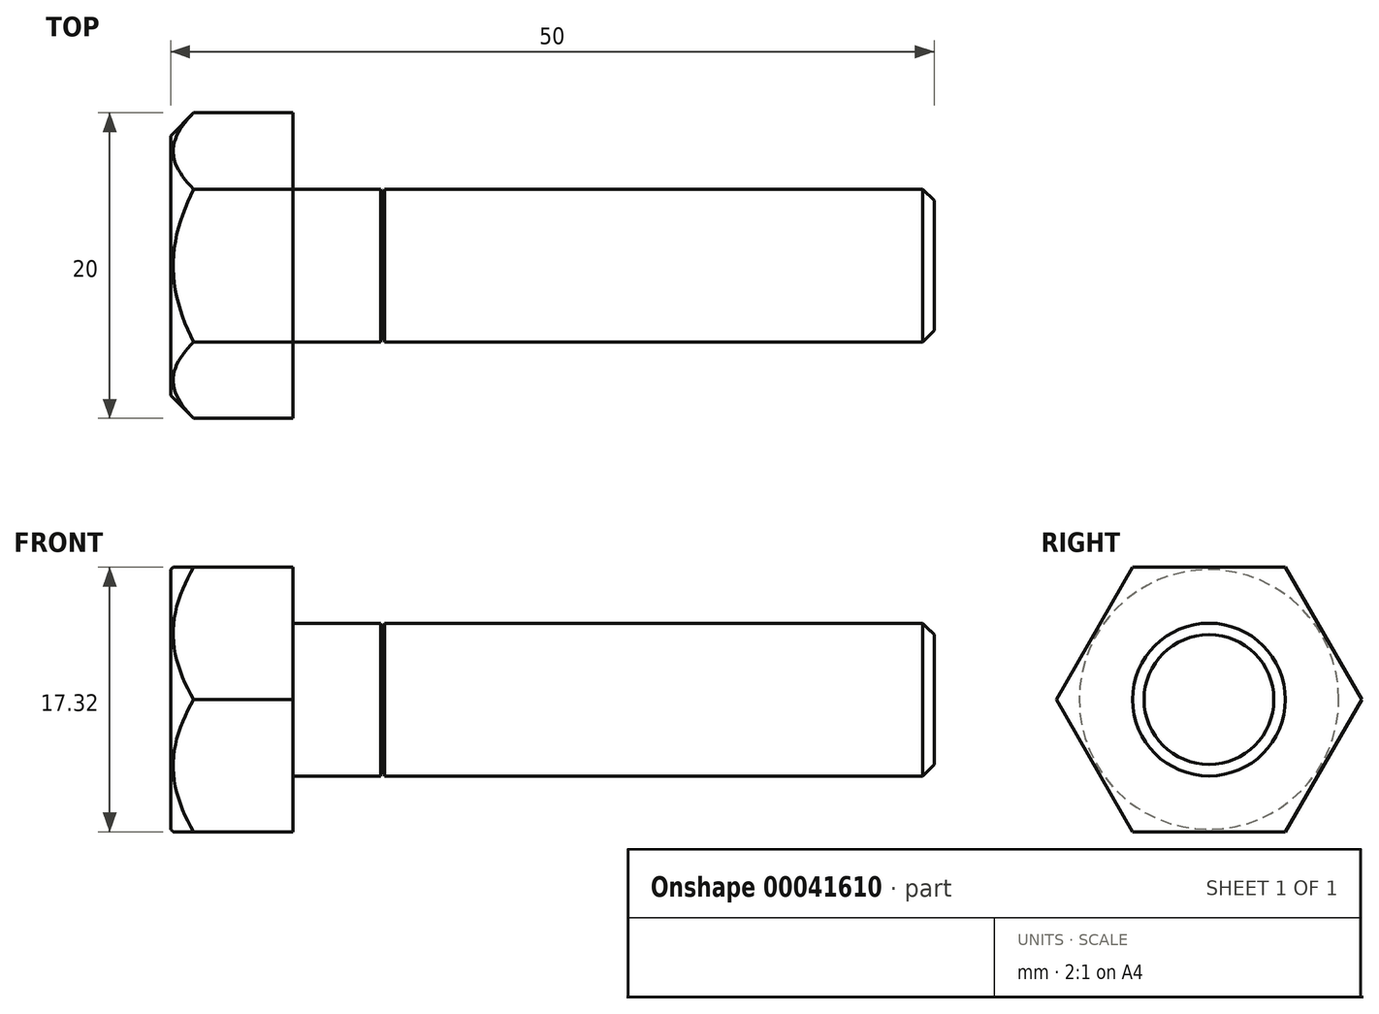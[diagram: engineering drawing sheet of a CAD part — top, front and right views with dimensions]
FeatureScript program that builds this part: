
annotation { "Feature Type Name" : "Feature", "Feature Type Description" : "" }
export const myFeature = defineFeature(function(context is Context, id is Id, definition is map)
    precondition{}
    {
        {
            var Q0;
            Q0=qCreatedBy(makeId("Front.planeOp"),FACE);
            var sketch = newSketch(context, id + "F0", { "sketchPlane" : qUnion([Q0])});
            skLineSegment(sketch, "E0.rect.bottom", {"start": v(8, 10) * mm, "end": v(0, 10) * mm});
            skLineSegment(sketch, "E0.rect.top", {"start": v(50, -10) * mm, "end": v(0, -10) * mm, "construction": true});
            skLineSegment(sketch, "E0.rect.left", {"start": v(50, 10) * mm, "end": v(50, -10) * mm, "construction": true});
            skLineSegment(sketch, "E0.rect.right", {"start": v(0, 10) * mm, "end": v(0, -10) * mm, "construction": true});
            skPoint(sketch, "E0.rect.middle", {"position": v(25, 0) * mm});
            skLineSegment(sketch, "E1", {"start": v(0, 0) * mm, "end": v(50, 0) * mm});
            skLineSegment(sketch, "E2", {"start": v(0, 10) * mm, "end": v(0, 0) * mm});
            skLineSegment(sketch, "E3", {"start": v(50, 4.25) * mm, "end": v(50, 0) * mm});
            skLineSegment(sketch, "E4", {"start": v(8, 10) * mm, "end": v(8, 5) * mm});
            skLineSegment(sketch, "E5", {"start": v(8, 5) * mm, "end": v(13.75, 5) * mm});
            skLineSegment(sketch, "E6", {"start": v(13.75, 5) * mm, "end": v(13.87, 4.25) * mm});
            skLineSegment(sketch, "E7", {"start": v(13.87, 4.25) * mm, "end": v(14, 5) * mm});
            skLineSegment(sketch, "E8", {"start": v(14, 5) * mm, "end": v(49.25, 5) * mm});
            skLineSegment(sketch, "E9", {"start": v(49.25, 5) * mm, "end": v(50, 4.25) * mm});
            skLineSegment(sketch, "E10", {"start": v(13.87, 4.25) * mm, "end": v(50, 4.25) * mm, "construction": true});
            skLineSegment(sketch, "E11", {"start": v(49.25, 5) * mm, "end": v(50, 5.75) * mm, "construction": true});
            skPoint(sketch, "E12", {"position": v(50, 4.25) * mm});
            skPoint(sketch, "E13", {"position": v(49.25, 5) * mm});
            skPoint(sketch, "E14", {"position": v(50, -4.25) * mm});
            skLineSegment(sketch, "E15", {"start": v(50, 0) * mm, "end": v(50, -4.25) * mm});
            skLineSegment(sketch, "E16", {"start": v(49.25, 5) * mm, "end": v(49.25, -5) * mm, "construction": true});
            skPoint(sketch, "E17", {"position": v(49.25, 0) * mm});
            skSolve(sketch);
        }
        {
            var Q0;
            Q0=makeQuery(id+"F0.imprint","IMPRINT",FACE,{"disambiguationData":[TD([[makeQuery(id+"F0.imprint","IMPRINT",EDGE,{"derivedFrom":sQuery(id+"F0.wireOp",EDGE,"E0.rect.bottom")}),1.0]])]});
            var Q1;
            Q1=sQuery(id+"F0.wireOp",EDGE,"E1");
            revolve(context, id + "F1", {"entities" : qUnion([Q0]), "axis" : qUnion([Q1]), "revolveType" : RevolveType.FULL});
        }
        {
            var Q0;
            Q0=makeQuery(id+"F1.opRevolve","SWEPT_EDGE",EDGE,{"disambiguationData":[OSD([sQuery(id+"F0.wireOp",EDGE,"E0.rect.bottom"),sQuery(id+"F0.wireOp",EDGE,"E2")])]});
            chamfer(context, id + "F2", {"entities" : qUnion([Q0]), "width" : 1.5 * mm, "tangentPropagation" : true});
        }
        {
            var Q0;
            Q0=makeQuery(id+"F1.opRevolve","SWEPT_FACE",FACE,{"disambiguationData":[OSD([sQuery(id+"F0.wireOp",EDGE,"E2")])]});
            var sketch = newSketch(context, id + "F3", { "sketchPlane" : qUnion([Q0])});
            skCircle(sketch, "E18.0", {"center": v(0, 0) * mm, "radius": 10 * mm});
            skCircle(sketch, "E19.cCircle", {"center": v(0, 0) * mm, "radius": 10 * mm, "construction": true});
            skLineSegment(sketch, "E19.0", {"start": v(-5, 8.66) * mm, "end": v(5, 8.66) * mm});
            skLineSegment(sketch, "E19.1", {"start": v(5, 8.66) * mm, "end": v(10, 0) * mm});
            skLineSegment(sketch, "E19.2", {"start": v(10, 0) * mm, "end": v(5, -8.66) * mm});
            skLineSegment(sketch, "E19.3", {"start": v(5, -8.66) * mm, "end": v(-5, -8.66) * mm});
            skLineSegment(sketch, "E19.4", {"start": v(-5, -8.66) * mm, "end": v(-10, 0) * mm});
            skLineSegment(sketch, "E19.5", {"start": v(-10, 0) * mm, "end": v(-5, 8.66) * mm});
            skSolve(sketch);
        }
        {
            var Q0;
            {var subQ0=sQuery(id+"F3.wireOp",EDGE,"E19.5");Q0=makeQuery(id+"F3.imprint","IMPRINT",FACE,{"disambiguationData":[TD([[makeQuery(id+"F3.imprint","IMPRINT",EDGE,{"derivedFrom":subQ0}),1.0]])]});}
            var Q1;
            {var subQ0=sQuery(id+"F3.wireOp",EDGE,"E19.0");Q1=makeQuery(id+"F3.imprint","IMPRINT",FACE,{"disambiguationData":[TD([[makeQuery(id+"F3.imprint","IMPRINT",EDGE,{"derivedFrom":subQ0}),1.0]])]});}
            var Q2;
            {var subQ0=sQuery(id+"F3.wireOp",EDGE,"E19.1");Q2=makeQuery(id+"F3.imprint","IMPRINT",FACE,{"disambiguationData":[TD([[makeQuery(id+"F3.imprint","IMPRINT",EDGE,{"derivedFrom":subQ0}),1.0]])]});}
            var Q3;
            {var subQ0=sQuery(id+"F3.wireOp",EDGE,"E19.2");Q3=makeQuery(id+"F3.imprint","IMPRINT",FACE,{"disambiguationData":[TD([[makeQuery(id+"F3.imprint","IMPRINT",EDGE,{"derivedFrom":subQ0}),1.0]])]});}
            var Q4;
            {var subQ0=sQuery(id+"F3.wireOp",EDGE,"E19.3");Q4=makeQuery(id+"F3.imprint","IMPRINT",FACE,{"disambiguationData":[TD([[makeQuery(id+"F3.imprint","IMPRINT",EDGE,{"derivedFrom":subQ0}),1.0]])]});}
            var Q5;
            {var subQ0=sQuery(id+"F3.wireOp",EDGE,"E19.4");Q5=makeQuery(id+"F3.imprint","IMPRINT",FACE,{"disambiguationData":[TD([[makeQuery(id+"F3.imprint","IMPRINT",EDGE,{"derivedFrom":subQ0}),1.0]])]});}
            extrude(context, id + "F4", {"entities" : qUnion([Q0, Q1, Q2, Q3, Q4, Q5]), "operationType" : NewBodyOperationType.REMOVE, "endBound" : BoundingType.THROUGH_ALL, "oppositeDirection" : true, "depth" : 25 * mm});
        }
    });
